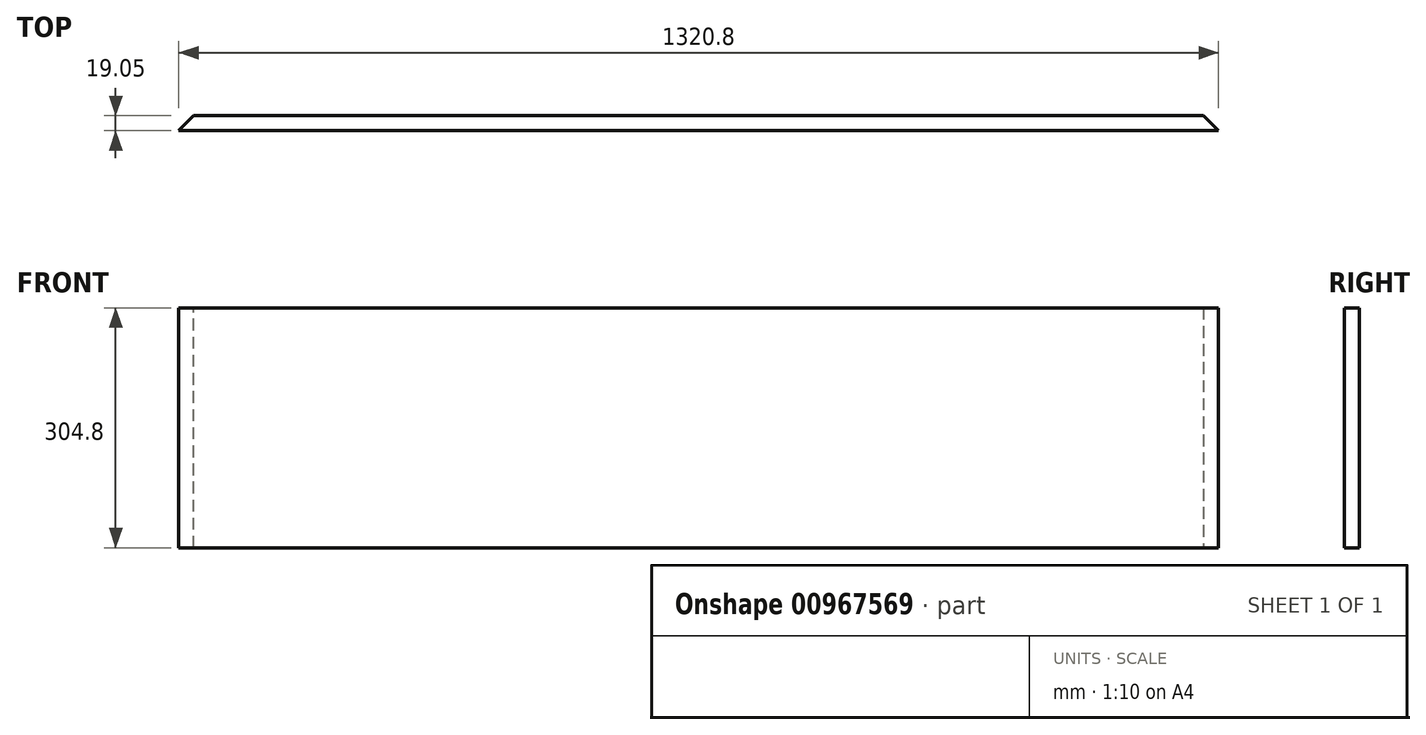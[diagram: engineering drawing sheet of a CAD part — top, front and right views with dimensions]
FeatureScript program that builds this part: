
annotation { "Feature Type Name" : "Feature", "Feature Type Description" : "" }
export const myFeature = defineFeature(function(context is Context, id is Id, definition is map)
    precondition{}
    {
        {
            var Q0;
            Q0=qCreatedBy(makeId("Front.planeOp"),FACE);
            var sketch = newSketch(context, id + "F0", { "sketchPlane" : qUnion([Q0])});
            skLineSegment(sketch, "E0.bottom", {"start": v(992.7, 140.63) * mm, "end": v(-328.1, 140.63) * mm});
            skLineSegment(sketch, "E0.top", {"start": v(992.7, -164.17) * mm, "end": v(-328.1, -164.17) * mm});
            skLineSegment(sketch, "E0.left", {"start": v(992.7, 140.63) * mm, "end": v(992.7, -164.17) * mm});
            skLineSegment(sketch, "E0.right", {"start": v(-328.1, 140.63) * mm, "end": v(-328.1, -164.17) * mm});
            skSolve(sketch);
        }
        {
            var Q0;
            Q0=makeQuery(id+"F0.imprint","IMPRINT",FACE,{"disambiguationData":[TD([[makeQuery(id+"F0.imprint","IMPRINT",EDGE,{"derivedFrom":sQuery(id+"F0.wireOp",EDGE,"E0.bottom")}),1.0]])]});
            extrude(context, id + "F1", {"entities" : qUnion([Q0]), "depth" : 19.05 * mm, "offsetDistance" : 25.4 * mm});
        }
        {
            var Q0;
            Q0=makeQuery(id+"F1.opExtrude","CAP_EDGE",EDGE,{"disambiguationData":[OSD([sQuery(id+"F0.wireOp",EDGE,"E0.right")])],"isStart":true});
            var Q1;
            Q1=makeQuery(id+"F1.opExtrude","CAP_EDGE",EDGE,{"disambiguationData":[OSD([sQuery(id+"F0.wireOp",EDGE,"E0.left")])],"isStart":true});
            chamfer(context, id + "F2", {"entities" : qUnion([Q0, Q1]), "width" : 19.05 * mm});
        }
    });
